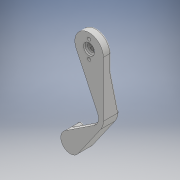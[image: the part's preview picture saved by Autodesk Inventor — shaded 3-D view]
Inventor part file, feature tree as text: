
AUTODESK INVENTOR PART (.ipt)
format: ipt  version: 2017 (Build 210142000, 142)  size: 347,136 bytes
history: native  units: mm
features: sketch x6, extrude x5, fillet x3, hole x2
ambient origin geometry x8: Origin, YZ Plane, XZ Plane, XY Plane, X Axis, Y Axis, Z Axis, Center Point
bodies: Solid1 (feature_tree)
feature tree (16):
  extrude  "Extrusion1"  Depth=9.0mm
  extrude  "Extrusion2"  Depth=6.0mm
  extrude  "Extrusion4"  Depth=25.0mm
  hole  "Hole1"  [1 undecoded]
  fillet  "Fillet1"  Radius=3.0mm
  fillet  "Fillet2"  Radius=9.0mm
  fillet  "Fillet4"  Radius=17.0mm
  extrude  "Extrusion5"  Depth=7.0mm TaperAngle=0.0deg
  hole  "Hole3"  [1 undecoded]
  extrude  "Extrusion6"  Depth=1.0mm
  sketch  "Sketch1"  dims[d0=35.0mm d2=9.0mm]
  sketch  "Sketch3"  dims[d4=9.0mm d7=6.0mm]
  sketch  "Sketch5"  dims[d8=6.108652mm d9=25.0mm]
  sketch  "Sketch6"  dims[d10=6.0mm d11=3.0mm d12=3.0mm d13=0.0mm d22=9.0mm d23=17.0mm]
  sketch  "Sketch8"  dims[d25=5.0mm d29=7.0mm d30=0.0mm]
  sketch  "Sketch9"  dims[d34=5.0mm d35=60.0mm d36=25.0mm d37=20.0mm d38=0.0mm d39=18.0mm d40=11.0mm d41=5.5mm d42=5.5mm d43=2.0mm d44=6.0mm d45=4.0mm d46=2.5mm d47=90.0deg d48=8.0mm d49=20.594885mm d52=3.0mm d62=2.0mm d63=2.0mm d65=1.0mm d66=5.0mm d67=10.0mm d68=0.0mm d82=10.0mm d83=10.0mm d71=7.0mm d72=6.0mm d73=4.0mm d74=2.0mm d75=90.0deg d76=1.0mm d77=20.594885mm d80=2.5mm d81=0.0mm d78=1.0mm d79=1.0mm]
note: 2 required parameter values undecoded (feature->parameter linkage not recoverable at this tier; creation-order binding heuristic only, values carry confidence <= 0.55)
